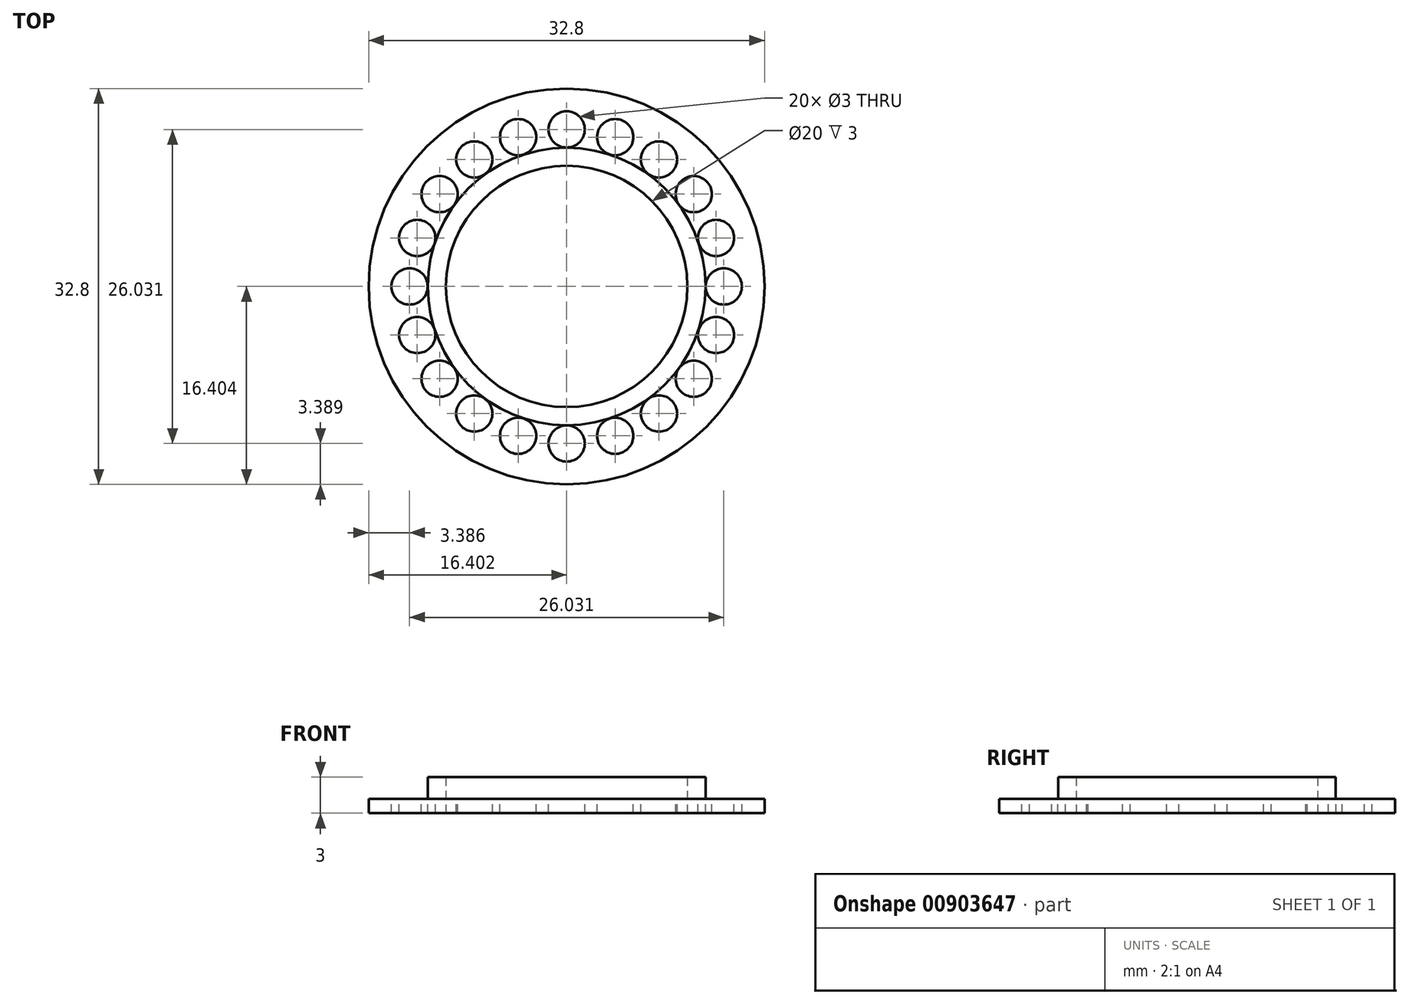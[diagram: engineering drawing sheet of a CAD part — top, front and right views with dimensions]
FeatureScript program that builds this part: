
annotation { "Feature Type Name" : "Feature", "Feature Type Description" : "" }
export const myFeature = defineFeature(function(context is Context, id is Id, definition is map)
    precondition{}
    {
        {
            var Q0;
            Q0=qCreatedBy(makeId("Top.planeOp"),FACE);
            var sketch = newSketch(context, id + "F0", { "sketchPlane" : qUnion([Q0])});
            skCircle(sketch, "E0", {"center": v(-45.6, 14.5) * mm, "radius": 10 * mm});
            skCircle(sketch, "E1", {"center": v(-45.6, 14.5) * mm, "radius": 16.4 * mm});
            skCircle(sketch, "E2", {"center": v(-45.6, 14.5) * mm, "radius": 11.5 * mm});
            skSolve(sketch);
        }
        {
            var Q0;
            Q0=makeQuery(id+"F0.imprint","IMPRINT",FACE,{"disambiguationData":[TD([[makeQuery(id+"F0.imprint","IMPRINT",EDGE,{"derivedFrom":sQuery(id+"F0.wireOp",EDGE,"E1")}),1.0]])]});
            extrude(context, id + "F1", {"entities" : qUnion([Q0]), "depth" : 1.2 * mm, "offsetDistance" : 25 * mm});
        }
        {
            var Q0;
            Q0=makeQuery(id+"F0.imprint","IMPRINT",FACE,{"disambiguationData":[TD([[makeQuery(id+"F0.imprint","IMPRINT",EDGE,{"derivedFrom":sQuery(id+"F0.wireOp",EDGE,"E0")}),-1.0]])]});
            extrude(context, id + "F2", {"entities" : qUnion([Q0]), "operationType" : NewBodyOperationType.ADD, "depth" : 3 * mm, "offsetDistance" : 25 * mm});
        }
        {
            var Q0;
            Q0=makeQuery(id+"F1.opExtrude","CAP_FACE",FACE,{"disambiguationData":[OSD([sQuery(id+"F0.wireOp",EDGE,"E1"),sQuery(id+"F0.wireOp",EDGE,"E2")])],"isStart":false});
            var sketch = newSketch(context, id + "F3", { "sketchPlane" : qUnion([Q0])});
            skCircle(sketch, "E3.0.0", {"center": v(-45.6, 14.5) * mm, "radius": 16.4 * mm, "construction": true});
            skCircle(sketch, "E4.0", {"center": v(-45.6, 14.5) * mm, "radius": 11.5 * mm, "construction": true});
            skLineSegment(sketch, "E5", {"start": v(-45.6, 14.5) * mm, "end": v(-45.6, 32.37) * mm, "construction": true});
            skCircle(sketch, "E6", {"center": v(-45.6, 27.52) * mm, "radius": 1.5 * mm});
            skCircle(sketch, "E7.1.0", {"center": v(-49.62, 26.88) * mm, "radius": 1.5 * mm});
            skCircle(sketch, "E7.2.0", {"center": v(-53.25, 25.03) * mm, "radius": 1.5 * mm});
            skCircle(sketch, "E7.3.0", {"center": v(-56.13, 22.15) * mm, "radius": 1.5 * mm});
            skCircle(sketch, "E7.4.0", {"center": v(-57.98, 18.53) * mm, "radius": 1.5 * mm});
            skCircle(sketch, "E7.5.0", {"center": v(-58.61, 14.5) * mm, "radius": 1.5 * mm});
            skCircle(sketch, "E7.6.0", {"center": v(-57.98, 10.48) * mm, "radius": 1.5 * mm});
            skCircle(sketch, "E7.7.0", {"center": v(-56.13, 6.85) * mm, "radius": 1.5 * mm});
            skCircle(sketch, "E7.8.0", {"center": v(-53.25, 3.97) * mm, "radius": 1.5 * mm});
            skCircle(sketch, "E7.9.0", {"center": v(-49.62, 2.13) * mm, "radius": 1.5 * mm});
            skCircle(sketch, "E7.10.0", {"center": v(-45.6, 1.49) * mm, "radius": 1.5 * mm});
            skCircle(sketch, "E7.11.0", {"center": v(-41.58, 2.13) * mm, "radius": 1.5 * mm});
            skCircle(sketch, "E7.12.0", {"center": v(-37.95, 3.97) * mm, "radius": 1.5 * mm});
            skCircle(sketch, "E7.13.0", {"center": v(-35.07, 6.85) * mm, "radius": 1.5 * mm});
            skCircle(sketch, "E7.14.0", {"center": v(-33.22, 10.48) * mm, "radius": 1.5 * mm});
            skCircle(sketch, "E7.15.0", {"center": v(-32.58, 14.5) * mm, "radius": 1.5 * mm});
            skCircle(sketch, "E7.16.0", {"center": v(-33.22, 18.53) * mm, "radius": 1.5 * mm});
            skCircle(sketch, "E7.17.0", {"center": v(-35.07, 22.15) * mm, "radius": 1.5 * mm});
            skCircle(sketch, "E7.18.0", {"center": v(-37.95, 25.03) * mm, "radius": 1.5 * mm});
            skCircle(sketch, "E7.19.0", {"center": v(-41.58, 26.88) * mm, "radius": 1.5 * mm});
            skSolve(sketch);
        }
        {
            var Q0;
            Q0 = qSketchRegion(id + "F3", true);
            extrude(context, id + "F4", {"entities" : qUnion([Q0]), "operationType" : NewBodyOperationType.REMOVE, "oppositeDirection" : true, "depth" : 25 * mm, "offsetDistance" : 25 * mm});
        }
    });
